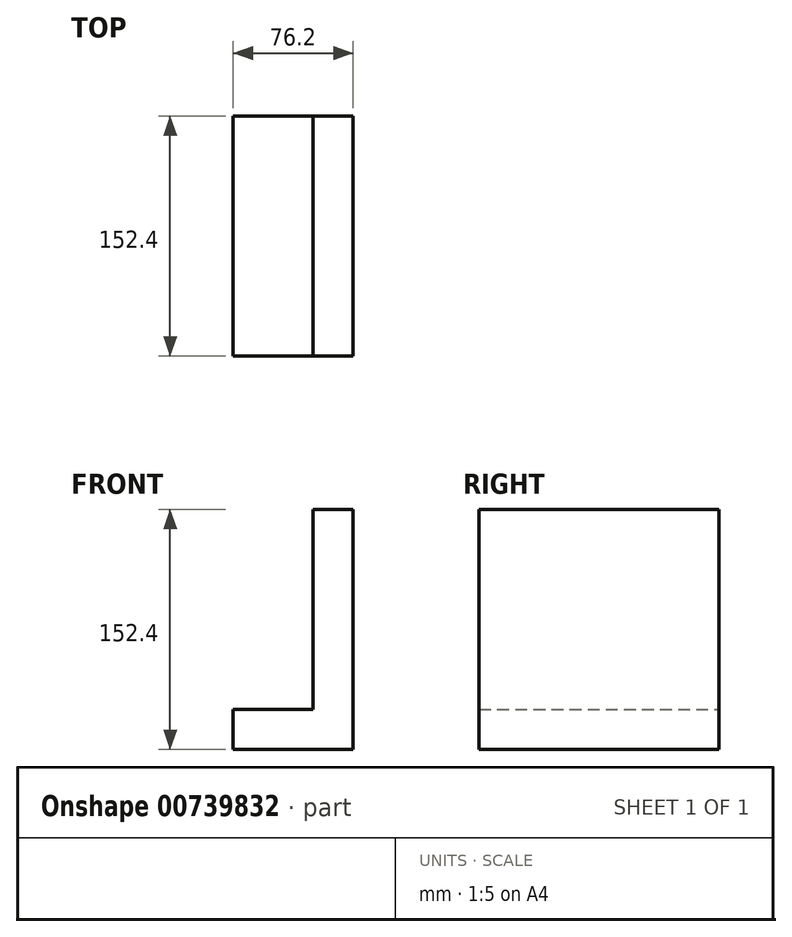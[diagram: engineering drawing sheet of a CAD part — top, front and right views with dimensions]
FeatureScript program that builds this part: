
annotation { "Feature Type Name" : "Feature", "Feature Type Description" : "" }
export const myFeature = defineFeature(function(context is Context, id is Id, definition is map)
    precondition{}
    {
        {
            var Q0;
            Q0=qCreatedBy(makeId("Front.planeOp"),FACE);
            var sketch = newSketch(context, id + "F0", { "sketchPlane" : qUnion([Q0])});
            skLineSegment(sketch, "E0", {"start": v(-25.4, 152.4) * mm, "end": v(0, 152.4) * mm});
            skLineSegment(sketch, "E1", {"start": v(0, 152.4) * mm, "end": v(0, 0) * mm});
            skLineSegment(sketch, "E2", {"start": v(0, 0) * mm, "end": v(-76.2, 0) * mm});
            skLineSegment(sketch, "E3", {"start": v(-76.2, 0) * mm, "end": v(-76.2, 25.4) * mm});
            skLineSegment(sketch, "E4", {"start": v(-76.2, 25.4) * mm, "end": v(-25.4, 25.4) * mm});
            skLineSegment(sketch, "E5", {"start": v(-25.4, 25.4) * mm, "end": v(-25.4, 152.4) * mm});
            skSolve(sketch);
        }
        {
            var Q0;
            Q0=makeQuery(id+"F0.imprint","IMPRINT",FACE,{"disambiguationData":[TD([[makeQuery(id+"F0.imprint","IMPRINT",EDGE,{"derivedFrom":sQuery(id+"F0.wireOp",EDGE,"E0")}),-1.0]])]});
            extrude(context, id + "F1", {"entities" : qUnion([Q0]), "endBound" : BoundingType.SYMMETRIC, "depth" : 152.4 * mm, "offsetDistance" : 25.4 * mm});
        }
    });
